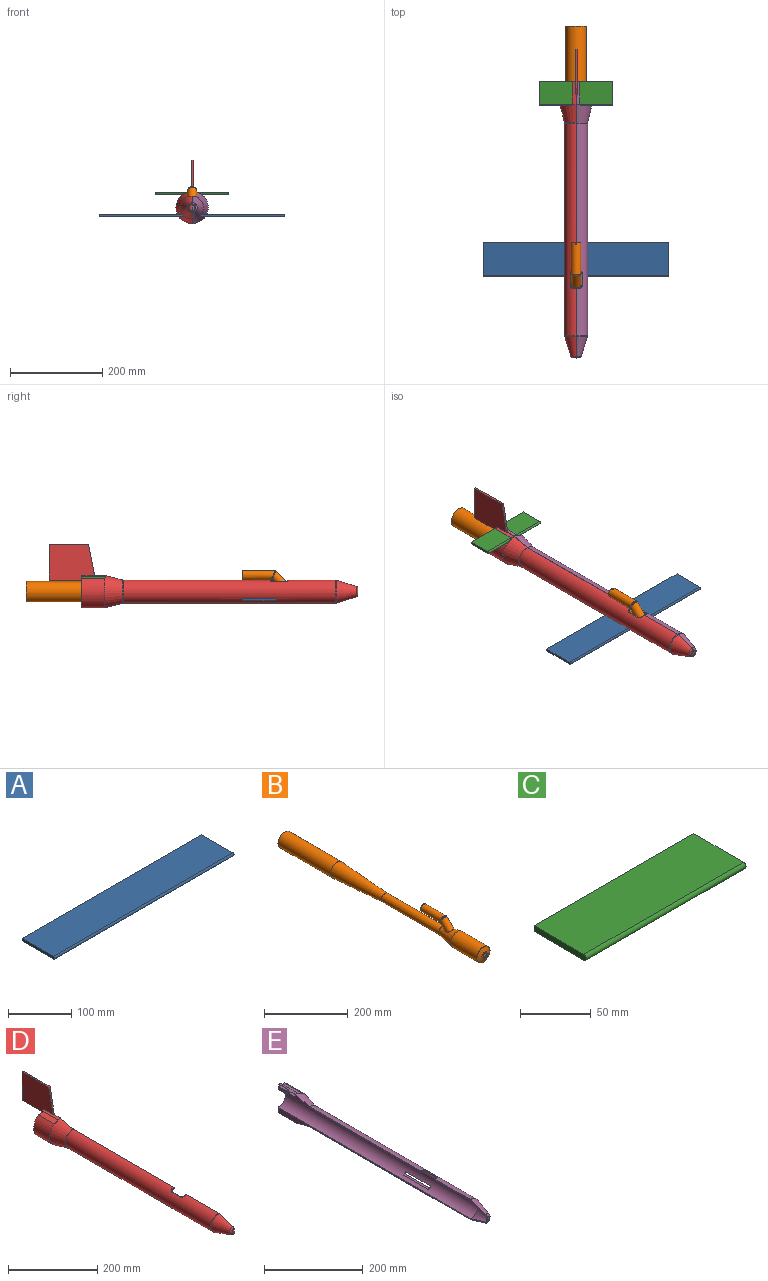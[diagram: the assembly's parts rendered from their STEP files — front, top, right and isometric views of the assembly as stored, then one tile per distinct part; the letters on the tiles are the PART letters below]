
ASSEMBLY  parts=5 mates=4
PART A: 6 faces, bbox 400x72.5x5 mm
  f0: plane 400x70mm, normal (0,0,1), area 28000mm2, adj f1,f3,f4,f5
  f1: cylinder r=2.5mm len=400mm, axis (-1,0,0), area 3141.6mm2, adj f0,f2,f4,f5
  f2: plane 400x70mm, normal (0,0,-1), area 28000mm2, adj f1,f3,f4,f5
  f3: plane 400x5mm, normal (0,1,0), area 2000mm2, adj f0,f2,f4,f5
  f4: plane 72.5x5mm, normal (1,0,0), area 359.8mm2, adj f0,f1,f2,f3
  f5: plane 72.5x5mm, normal (-1,0,0), area 359.8mm2, adj f0,f1,f2,f3
PART B: 31 faces, bbox 45.1x680.1x68.9 mm
  f0: cone r=22.23mm half-angle=74.1deg, axis (0,1,0), area 1381.2mm2, adj f5,f24,f25,f26,f28,f29,f30
  f1: cone r=22.23mm half-angle=11.4deg, axis (0,-1,0), area 5146.1mm2, adj f4,f5,f16
  f2: cylinder r=22.23mm len=177.8mm, axis (0,1,0), area 24828.7mm2, adj f3,f12
  f3: cone r=11.94mm half-angle=3.6deg, axis (0,1,0), area 17413.8mm2, adj f2,f4
  f4: cylinder r=11.94mm len=193.68mm, axis (0,1,0), area 14527.3mm2, adj f1,f3
  f5: cylinder r=22.23mm len=88.9mm, axis (0,1,0), area 12414.3mm2, adj f0,f1
  f6: cone r=0mm half-angle=74.1deg, axis (0,1,0), area 1229.8mm2, adj f7,f23
  f7: cylinder r=20.62mm len=87.69mm, axis (0,1,0), area 11364.2mm2, adj f6,f8
  f8: cone r=20.62mm half-angle=11.4deg, axis (0,-1,0), area 4677.6mm2, adj f7,f9,f13,f14,f15
  f9: cylinder r=10.34mm len=193.68mm, axis (0,1,0), area 12580.3mm2, adj f8,f10
  f10: cone r=10.34mm half-angle=3.6deg, axis (0,1,0), area 15782.7mm2, adj f9,f11
  f11: cylinder r=20.62mm len=177.8mm, axis (0,1,0), area 23041.2mm2, adj f10,f12
  f12: plane 44.45x44.45mm, normal (0,1,0), area 215.4mm2, adj f2,f11
  f13: cylinder r=10.29mm len=20.57mm, axis (0,0.71,0.71), area 224.7mm2, adj f8,f14
  f14: cone r=10.29mm half-angle=56.4deg, axis (0,-0.71,-0.71), area 61.9mm2, adj f8,f13,f15
  f15: cylinder r=8.69mm len=39.3mm, axis (0,0.71,0.71), area 1820.3mm2, adj f8,f14,f17
  f16: cylinder r=10.29mm len=39.98mm, axis (0,0.71,0.71), area 1771.8mm2, adj f1,f20,f21
  f17: cylinder r=8.69mm len=70.5mm, axis (0,1,0), area 3648.4mm2, adj f15,f18,f22
  f18: plane 20.57x20.57mm, normal (0,1,0), area 95.4mm2, adj f17,f19
  f19: cylinder r=10.29mm len=69.09mm, axis (0,1,0), area 4226mm2, adj f18,f20,f21,f22
  f20: bspline ~20.57x11.75mm, area 83mm2, adj f16,f19
  f21: bspline ~20.57x10.29mm, area 80.9mm2, adj f16,f19
  f22: cylinder r=1mm len=2mm, axis (0,0,1), area 10.1mm2, adj f17,f19
  f23: cylinder r=7mm len=14mm, axis (0,-1,0), area 161.2mm2, adj f6,f27
  f24: plane 8x4.62mm, normal (0.87,0,0.5), area 22.2mm2, adj f0,f25,f27,f28
  f25: plane 9.94x3.34mm, normal (0,0,1), area 22.2mm2, adj f0,f24,f26,f27
  f26: plane 8x4.62mm, normal (-0.87,0,0.5), area 22.2mm2, adj f0,f25,f27,f29
  f27: plane 18.48x16mm, normal (0,-1,0), area 67.8mm2, adj f23,f24,f25,f26,f28,f29,f30
  f28: plane 8x4.62mm, normal (0.87,0,-0.5), area 22.2mm2, adj f0,f24,f27,f30
  f29: plane 8x4.62mm, normal (-0.87,0,-0.5), area 22.2mm2, adj f0,f26,f27,f30
  f30: plane 9.24x2.64mm, normal (0,0,-1), area 22.2mm2, adj f0,f27,f28,f29
PART C: 6 faces, bbox 160x52.5x5 mm
  f0: plane 160x5mm, normal (0,1,0), area 800mm2, adj f1,f3,f4,f5
  f1: plane 160x50mm, normal (0,0,1), area 8000mm2, adj f0,f2,f4,f5
  f2: cylinder r=2.5mm len=160mm, axis (-1,0,0), area 1256.6mm2, adj f1,f3,f4,f5
  f3: plane 160x50mm, normal (0,0,-1), area 8000mm2, adj f0,f2,f4,f5
  f4: plane 52.5x5mm, normal (1,0,0), area 259.8mm2, adj f0,f1,f2,f3
  f5: plane 52.5x5mm, normal (-1,0,0), area 259.8mm2, adj f0,f1,f2,f3
PART D: 43 faces, bbox 39.9x670x140.9 mm
  f0: plane 411.37x12.7mm, normal (1,0,0), area 1408.2mm2, adj f2,f4,f7,f8,f9,f13,f17,f18
  f1: plane 6.31x0.94mm, normal (0,1,0), area 3.6mm2, adj f2,f6,f31
  f2: cylinder r=35mm len=49.38mm, axis (0,1,0), area 358mm2, adj f0,f1,f4,f6,f17,f29,f31
  f3: torus R=30mm, axis (0,-1,0), area 109.9mm2, adj f10,f11,f13,f29
  f4: plane 69.01x13.27mm, normal (0,-0.98,0.19), area 279.1mm2, adj f0,f2,f5,f6,f24,f31
  f5: plane 100x78mm, normal (1,0,0), area 7066.2mm2, adj f4,f21,f22,f23,f24,f30,f31,f32
  f6: plane 98.09x78mm, normal (-1,0,0), area 6921.2mm2, adj f1,f2,f4,f9,f22,f23,f24,f30
  f7: cylinder r=22.3mm len=552.3mm, axis (0,1,0), area 37667mm2, adj f0,f9,f11,f12,f25,f26,f27,f28
  f8: cylinder r=25mm len=460.92mm, axis (0,1,0), area 35209.2mm2, adj f0,f11,f18,f19,f25,f26,f27,f28
  f9: plane 64x35mm, normal (0,1,0), area 1055.2mm2, adj f0,f6,f7,f10,f11,f22,f32
  f10: cylinder r=35mm len=64.03mm, axis (0,1,0), area 4403mm2, adj f3,f9,f11,f29,f32
  f11: plane 600x60mm, normal (1,0,0), area 2771.7mm2, adj f3,f7,f8,f9,f10,f12,f13,f14
  f12: cone r=8.24mm half-angle=17.5deg, axis (0,1,0), area 2248mm2, adj f7,f11,f16
  f13: cone r=35mm half-angle=14deg, axis (0,1,0), area 3769.9mm2, adj f0,f3,f11,f17,f18,f29
  f14: cone r=10mm half-angle=17.5deg, axis (0,1,0), area 2567.3mm2, adj f11,f19,f20
  f15: plane 12.66x6.33mm, normal (0,-1,0), area 63mm2, adj f11,f20
  f16: plane 16.49x8.24mm, normal (0,1,0), area 106.7mm2, adj f11,f12
  f17: torus R=30mm, axis (0,-1,0), area 11.4mm2, adj f0,f2,f13,f29
  f18: torus R=30mm, axis (0,1,0), area 96.4mm2, adj f0,f8,f11,f13
  f19: torus R=20mm, axis (0,-1,0), area 119.3mm2, adj f8,f11,f14
  f20: torus R=6.33mm, axis (0,1,0), area 180.9mm2, adj f11,f14,f15
  f21: plane 4x2mm, normal (0,-0.98,0.19), area 8.1mm2, adj f0,f5,f22,f32
  f22: plane 100x4mm, normal (0,0,-1), area 340mm2, adj f0,f5,f6,f9,f21,f23
  f23: plane 78x4mm, normal (0,1,0), area 312mm2, adj f5,f6,f22,f24
  f24: plane 85x4mm, normal (0,0,1), area 340mm2, adj f4,f5,f6,f23
  f25: plane 70x3.5mm, normal (0,0,-1), area 244.9mm2, adj f7,f8,f26,f28
  f26: cylinder r=2.5mm len=10.14mm, axis (1,0,0), area 33.9mm2, adj f7,f8,f25,f27
  f27: plane 70x5.14mm, normal (0,0,1), area 359.6mm2, adj f7,f8,f26,f28
  f28: plane 10.14x5mm, normal (0,-1,0), area 20.6mm2, adj f7,f8,f25,f27
  f29: cylinder r=2.5mm len=19.6mm, axis (1,0,0), area 110.8mm2, adj f0,f2,f3,f10,f13,f17,f31,f32
  f30: plane 5x4mm, normal (0,-1,0), area 20mm2, adj f5,f6,f31,f32
  f31: plane 50x10.31mm, normal (0,0,-1), area 467.6mm2, adj f0,f1,f2,f4,f5,f6,f29,f30
  f32: plane 50x21.6mm, normal (0,0,1), area 1022.7mm2, adj f0,f5,f6,f9,f10,f21,f29,f30
  f33: torus R=23.4mm, axis (0,-1,0), area 14.7mm2, adj f0,f8,f34,f36
  f34: torus R=23.9mm, axis (0,-1,0), area 13.9mm2, adj f0,f7,f33,f35,f36
  f35: bspline ~8.07x7.07mm, area 19.5mm2, adj f7,f34,f36,f37
  f36: bspline ~8.11x8.07mm, area 20.8mm2, adj f8,f33,f34,f35,f38
  f37: cylinder r=1.6mm len=26.3mm, axis (0,1,0), area 56.7mm2, adj f7,f35,f38,f39
  f38: cylinder r=1.6mm len=26.3mm, axis (0,1,0), area 62.4mm2, adj f8,f36,f37,f40
  f39: bspline ~8.07x7.07mm, area 19.5mm2, adj f7,f37,f40,f41
  f40: bspline ~8.11x8.07mm, area 20.8mm2, adj f8,f38,f39,f41,f42
  f41: torus R=23.9mm, axis (0,-1,0), area 13.9mm2, adj f7,f11,f39,f40,f42
  f42: torus R=23.4mm, axis (0,-1,0), area 14.7mm2, adj f8,f11,f40,f41
PART E: 37 faces, bbox 35x600x70 mm
  f0: cylinder r=35mm len=50mm, axis (0,-1,0), area 349.5mm2, adj f1,f2,f3,f4,f10,f24,f25
  f1: plane 411.37x12.7mm, normal (-1,0,0), area 1408.2mm2, adj f0,f3,f5,f6,f9,f10,f15,f17
  f2: plane 5.81x0.91mm, normal (0,1,0), area 3.1mm2, adj f0,f4,f25
  f3: plane 2.51x1.01mm, normal (0,0.98,-0.19), area 2.5mm2, adj f0,f1,f4,f25
  f4: plane 28.27x0.91mm, normal (-1,0,0), area 25.7mm2, adj f0,f2,f3,f25
  f5: cylinder r=25mm len=461.54mm, axis (0,-1,0), area 35257.6mm2, adj f1,f10,f14,f18,f20,f21,f22,f23
  f6: cylinder r=22.3mm len=552.3mm, axis (0,-1,0), area 37667mm2, adj f1,f8,f9,f14,f20,f21,f22,f23
  f7: cylinder r=35mm len=64.21mm, axis (0,-1,0), area 4458mm2, adj f9,f10,f14,f24,f26
  f8: cone r=8.24mm half-angle=17.5deg, axis (0,1,0), area 2248mm2, adj f6,f13,f14
  f9: plane 64x35mm, normal (0,1,0), area 1053.2mm2, adj f1,f6,f7,f14,f16,f17,f26
  f10: cone r=35mm half-angle=14deg, axis (0,1,0), area 3885.9mm2, adj f0,f1,f5,f7,f14,f24
  f11: cone r=10mm half-angle=17.5deg, axis (0,1,0), area 2567.3mm2, adj f14,f18,f19
  f12: plane 12.66x6.33mm, normal (0,-1,0), area 63mm2, adj f14,f19
  f13: plane 16.49x8.24mm, normal (0,1,0), area 106.7mm2, adj f8,f14
  f14: plane 600x60mm, normal (-1,0,0), area 2771.7mm2, adj f5,f6,f7,f8,f9,f10,f11,f12
  f15: plane 4x2.5mm, normal (0,0.98,-0.19), area 10.2mm2, adj f1,f16,f17,f26
  f16: plane 30x4mm, normal (-1,0,0), area 118.5mm2, adj f9,f15,f17,f26
  f17: plane 30x2.5mm, normal (0,0,1), area 75mm2, adj f1,f9,f15,f16
  f18: torus R=20mm, axis (0,1,0), area 119.3mm2, adj f5,f11,f14
  f19: torus R=6.33mm, axis (0,-1,0), area 180.9mm2, adj f11,f12,f14
  f20: plane 70x3.5mm, normal (0,0,-1), area 244.9mm2, adj f5,f6,f21,f23
  f21: cylinder r=2.5mm len=10.14mm, axis (1,0,0), area 33.9mm2, adj f5,f6,f20,f22
  f22: plane 70x5.14mm, normal (0,0,1), area 359.6mm2, adj f5,f6,f21,f23
  f23: plane 10.14x5mm, normal (0,-1,0), area 20.6mm2, adj f5,f6,f20,f22
  f24: cylinder r=2.5mm len=19.6mm, axis (1,0,0), area 111.3mm2, adj f0,f1,f7,f10,f25,f26
  f25: plane 49x8.31mm, normal (0,0,-1), area 336.4mm2, adj f0,f1,f2,f3,f4,f24
  f26: plane 49x19.6mm, normal (0,0,1), area 887.1mm2, adj f1,f7,f9,f15,f16,f24
  f27: bspline ~8.07x7.07mm, area 19.5mm2, adj f6,f28,f30,f31
  f28: torus R=23.9mm, axis (0,-1,0), area 13.9mm2, adj f1,f6,f27,f29,f31
  f29: torus R=23.4mm, axis (0,-1,0), area 14.7mm2, adj f1,f5,f28,f31
  f30: cylinder r=1.6mm len=26.3mm, axis (0,-1,0), area 56.7mm2, adj f6,f27,f32,f33
  f31: bspline ~8.11x8.07mm, area 20.8mm2, adj f5,f27,f28,f29,f33
  f32: bspline ~8.07x7.07mm, area 19.5mm2, adj f6,f30,f34,f35
  f33: cylinder r=1.6mm len=26.3mm, axis (0,-1,0), area 62.4mm2, adj f5,f30,f31,f35
  f34: torus R=23.9mm, axis (0,-1,0), area 13.9mm2, adj f6,f14,f32,f35,f36
  f35: bspline ~8.11x8.07mm, area 20.8mm2, adj f5,f32,f33,f34,f36
  f36: torus R=23.4mm, axis (0,-1,0), area 14.7mm2, adj f5,f14,f34,f35
PLACE A t=(-0.2,360,0)mm
PLACE B t=(0,379.48,0)mm
PLACE C t=(0,360,0)mm
PLACE D t=(0,360,0)mm
PLACE E t=(0,360,0)mm
MATE fastened B.f0 <-> D.f2  axis (0,1,0) through (0,47.7,0)mm
MATE fastened E.f14 <-> D.f11  axis (-1,0,0) through (0,47.7,22.3)mm
MATE fastened A.f1 <-> E.f21  axis (-1,0,0) through (-0.2,180,-17.5)mm
MATE fastened C.f2 <-> E.f24  axis (-1,0,0) through (0,551,31.5)mm
